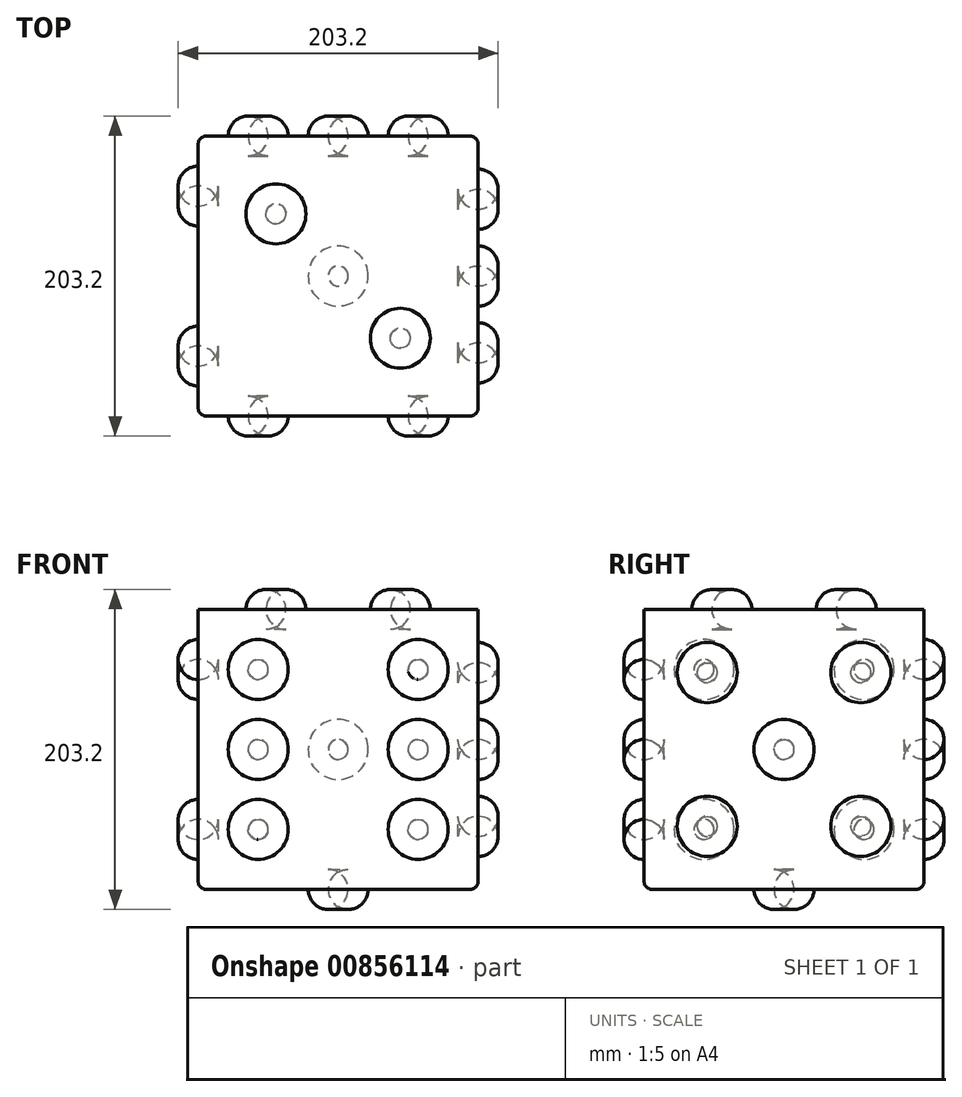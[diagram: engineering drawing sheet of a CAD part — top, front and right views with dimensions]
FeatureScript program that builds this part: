
annotation { "Feature Type Name" : "Feature", "Feature Type Description" : "" }
export const myFeature = defineFeature(function(context is Context, id is Id, definition is map)
    precondition{}
    {
        {
            var Q0;
            Q0=qCreatedBy(makeId("Top.planeOp"),FACE);
            var sketch = newSketch(context, id + "F0", { "sketchPlane" : qUnion([Q0])});
            skCircle(sketch, "E0", {"center": v(0, 0) * mm, "radius": 127 * mm});
            skSolve(sketch);
        }
        {
            var Q0;
            Q0 = qSketchRegion(id + "F0", true);
            extrude(context, id + "F1", {"entities" : qUnion([Q0]), "depth" : 177.8 * mm, "offsetDistance" : 25.4 * mm});
        }
        {
            var Q0;
            Q0=makeQuery(id+"F1.opExtrude","CAP_FACE",FACE,{"disambiguationData":[OSD([sQuery(id+"F0.wireOp",EDGE,"E0")])],"isStart":false});
            var sketch = newSketch(context, id + "F2", { "sketchPlane" : qUnion([Q0])});
            skLineSegment(sketch, "E1.bottom", {"start": v(-88.9, -88.9) * mm, "end": v(88.9, -88.9) * mm});
            skLineSegment(sketch, "E1.top", {"start": v(-88.9, 88.9) * mm, "end": v(88.9, 88.9) * mm});
            skLineSegment(sketch, "E1.left", {"start": v(-88.9, -88.9) * mm, "end": v(-88.9, 88.9) * mm});
            skLineSegment(sketch, "E1.right", {"start": v(88.9, -88.9) * mm, "end": v(88.9, 88.9) * mm});
            skPoint(sketch, "E1.middle", {"position": v(0, 0) * mm});
            skSolve(sketch);
        }
        {
            var Q0;
            {var subQ0=sQuery(id+"F2.wireOp",EDGE,"E1.top");Q0=makeQuery(id+"F2.imprint","IMPRINT",FACE,{"disambiguationData":[TD([[makeQuery(id+"F2.imprint","IMPRINT",EDGE,{"derivedFrom":subQ0}),1.0]])]});}
            var Q1;
            {var subQ0=sQuery(id+"F2.wireOp",EDGE,"E1.left");Q1=makeQuery(id+"F2.imprint","IMPRINT",FACE,{"disambiguationData":[TD([[makeQuery(id+"F2.imprint","IMPRINT",EDGE,{"derivedFrom":subQ0}),1.0]])]});}
            var Q2;
            {var subQ0=sQuery(id+"F2.wireOp",EDGE,"E1.bottom");Q2=makeQuery(id+"F2.imprint","IMPRINT",FACE,{"disambiguationData":[TD([[makeQuery(id+"F2.imprint","IMPRINT",EDGE,{"derivedFrom":subQ0}),-1.0]])]});}
            var Q3;
            {var subQ0=sQuery(id+"F2.wireOp",EDGE,"E1.right");Q3=makeQuery(id+"F2.imprint","IMPRINT",FACE,{"disambiguationData":[TD([[makeQuery(id+"F2.imprint","IMPRINT",EDGE,{"derivedFrom":subQ0}),-1.0]])]});}
            extrude(context, id + "F3", {"entities" : qUnion([Q0, Q1, Q2, Q3]), "operationType" : NewBodyOperationType.REMOVE, "endBound" : BoundingType.THROUGH_ALL, "oppositeDirection" : true, "depth" : 25.4 * mm, "offsetDistance" : 25.4 * mm});
        }
        {
            var Q0;
            Q0=makeQuery(id+"F3.boolean.opBoolean","COPY",FACE,{"derivedFrom":makeQuery(id+"F3.opExtrude","SWEPT_FACE",FACE,{"disambiguationData":[OSD([sQuery(id+"F2.wireOp",EDGE,"E1.right")])]})});
            var sketch = newSketch(context, id + "F4", { "sketchPlane" : qUnion([Q0])});
            skCircle(sketch, "E2", {"center": v(0, 88.9) * mm, "radius": 19.12 * mm});
            skCircle(sketch, "E3", {"center": v(48.8, 40.1) * mm, "radius": 19.12 * mm});
            skCircle(sketch, "E4", {"center": v(48.8, 137.7) * mm, "radius": 19.12 * mm});
            skCircle(sketch, "E5", {"center": v(-48.8, 137.7) * mm, "radius": 19.12 * mm});
            skCircle(sketch, "E6", {"center": v(-48.8, 40.1) * mm, "radius": 19.12 * mm});
            skLineSegment(sketch, "E7", {"start": v(48.8, 137.7) * mm, "end": v(-48.8, 40.1) * mm, "construction": true});
            skLineSegment(sketch, "E8", {"start": v(48.8, 40.1) * mm, "end": v(-48.8, 137.7) * mm, "construction": true});
            skSolve(sketch);
        }
        {
            var Q0;
            Q0=makeQuery(id+"F4.imprint","IMPRINT",FACE,{"disambiguationData":[TD([[makeQuery(id+"F4.imprint","IMPRINT",EDGE,{"derivedFrom":sQuery(id+"F4.wireOp",EDGE,"E5")}),1.0]])]});
            var Q1;
            Q1=makeQuery(id+"F4.imprint","IMPRINT",FACE,{"disambiguationData":[TD([[makeQuery(id+"F4.imprint","IMPRINT",EDGE,{"derivedFrom":sQuery(id+"F4.wireOp",EDGE,"E2")}),1.0]])]});
            var Q2;
            Q2=makeQuery(id+"F4.imprint","IMPRINT",FACE,{"disambiguationData":[TD([[makeQuery(id+"F4.imprint","IMPRINT",EDGE,{"derivedFrom":sQuery(id+"F4.wireOp",EDGE,"E4")}),1.0]])]});
            var Q3;
            Q3=makeQuery(id+"F4.imprint","IMPRINT",FACE,{"disambiguationData":[TD([[makeQuery(id+"F4.imprint","IMPRINT",EDGE,{"derivedFrom":sQuery(id+"F4.wireOp",EDGE,"E3")}),1.0]])]});
            var Q4;
            Q4=makeQuery(id+"F4.imprint","IMPRINT",FACE,{"disambiguationData":[TD([[makeQuery(id+"F4.imprint","IMPRINT",EDGE,{"derivedFrom":sQuery(id+"F4.wireOp",EDGE,"E6")}),1.0]])]});
            var Q5;
            Q5=sQuery(id+"F4.wireOp",EDGE,"E7");
            var Q6;
            Q6=sQuery(id+"F4.wireOp",EDGE,"E8");
            extrude(context, id + "F5", {"entities" : qUnion([Q0, Q1, Q2, Q3, Q4]), "operationType" : NewBodyOperationType.REMOVE, "surfaceEntities" : qUnion([Q5, Q6]), "oppositeDirection" : true, "depth" : 12.7 * mm, "offsetDistance" : 25.4 * mm});
        }
        {
            var Q0;
            Q0=makeQuery(id+"F3.boolean.opBoolean","COPY",FACE,{"derivedFrom":makeQuery(id+"F3.opExtrude","SWEPT_FACE",FACE,{"disambiguationData":[OSD([sQuery(id+"F2.wireOp",EDGE,"E1.bottom")])]})});
            var sketch = newSketch(context, id + "F6", { "sketchPlane" : qUnion([Q0])});
            skCircle(sketch, "E9", {"center": v(-50.8, 139.7) * mm, "radius": 19.05 * mm});
            skCircle(sketch, "E10", {"center": v(-50.8, 88.9) * mm, "radius": 19.05 * mm});
            skCircle(sketch, "E11", {"center": v(-50.8, 38.1) * mm, "radius": 19.05 * mm});
            skCircle(sketch, "E12", {"center": v(50.8, 139.7) * mm, "radius": 19.05 * mm});
            skCircle(sketch, "E13", {"center": v(50.8, 88.9) * mm, "radius": 19.05 * mm});
            skLineSegment(sketch, "E14", {"start": v(-50.8, 139.7) * mm, "end": v(-50.8, 88.9) * mm, "construction": true});
            skLineSegment(sketch, "E15", {"start": v(-50.8, 88.9) * mm, "end": v(-50.8, 38.1) * mm, "construction": true});
            skPoint(sketch, "E16", {"position": v(0, 0) * mm});
            skCircle(sketch, "E17", {"center": v(50.8, 38.1) * mm, "radius": 19.05 * mm});
            skSolve(sketch);
        }
        {
            var Q0;
            Q0=makeQuery(id+"F6.imprint","IMPRINT",FACE,{"disambiguationData":[TD([[makeQuery(id+"F6.imprint","IMPRINT",EDGE,{"derivedFrom":sQuery(id+"F6.wireOp",EDGE,"E10")}),1.0]])]});
            var Q1;
            Q1=makeQuery(id+"F6.imprint","IMPRINT",FACE,{"disambiguationData":[TD([[makeQuery(id+"F6.imprint","IMPRINT",EDGE,{"derivedFrom":sQuery(id+"F6.wireOp",EDGE,"E13")}),1.0]])]});
            var Q2;
            {var subQ0=sQuery(id+"F6.wireOp",EDGE,"E11");var subQ1=sQuery(id+"F2.wireOp",EDGE,"E1.bottom");var subQ2=makeQuery(id+"F6.imprint","INTERSECT",VERTEX,{"derivedFrom":[makeQuery(id+"F3.boolean.opBoolean","INTERSECT",EDGE,{"derivedFrom":[makeQuery(id+"F1.opExtrude","CAP_FACE",FACE,{"disambiguationData":[OSD([sQuery(id+"F0.wireOp",EDGE,"E0")])],"isStart":true}),makeQuery(id+"F3.opExtrude","SWEPT_FACE",FACE,{"disambiguationData":[OSD([subQ1])]})]}),subQ0]});Q2=makeQuery(id+"F6.imprint","IMPRINT",FACE,{"disambiguationData":[TD([[makeQuery(id+"F6.imprint","IMPRINT",EDGE,{"disambiguationData":[TD([[subQ2,1.0]])],"derivedFrom":subQ0}),1.0]])]});}
            var Q3;
            {var subQ0=sQuery(id+"F6.wireOp",EDGE,"E12");var subQ1=sQuery(id+"F2.wireOp",EDGE,"E1.bottom");var subQ2=makeQuery(id+"F6.imprint","INTERSECT",VERTEX,{"derivedFrom":[makeQuery(id+"F3.boolean.opBoolean","COPY",EDGE,{"derivedFrom":makeQuery(id+"F3.opExtrude","CAP_EDGE",EDGE,{"disambiguationData":[OSD([subQ1])],"isStart":true})}),subQ0]});Q3=makeQuery(id+"F6.imprint","IMPRINT",FACE,{"disambiguationData":[TD([[makeQuery(id+"F6.imprint","IMPRINT",EDGE,{"disambiguationData":[TD([[subQ2,1.0]])],"derivedFrom":subQ0}),1.0]])]});}
            var Q4;
            {var subQ0=sQuery(id+"F6.wireOp",EDGE,"E17");var subQ1=sQuery(id+"F2.wireOp",EDGE,"E1.bottom");var subQ2=makeQuery(id+"F6.imprint","INTERSECT",VERTEX,{"derivedFrom":[makeQuery(id+"F3.boolean.opBoolean","INTERSECT",EDGE,{"derivedFrom":[makeQuery(id+"F1.opExtrude","CAP_FACE",FACE,{"disambiguationData":[OSD([sQuery(id+"F0.wireOp",EDGE,"E0")])],"isStart":true}),makeQuery(id+"F3.opExtrude","SWEPT_FACE",FACE,{"disambiguationData":[OSD([subQ1])]})]}),subQ0]});Q4=makeQuery(id+"F6.imprint","IMPRINT",FACE,{"disambiguationData":[TD([[makeQuery(id+"F6.imprint","IMPRINT",EDGE,{"disambiguationData":[TD([[subQ2,1.0]])],"derivedFrom":subQ0}),1.0]])]});}
            var Q5;
            {var subQ0=sQuery(id+"F6.wireOp",EDGE,"E9");var subQ1=sQuery(id+"F2.wireOp",EDGE,"E1.bottom");var subQ2=makeQuery(id+"F6.imprint","INTERSECT",VERTEX,{"derivedFrom":[makeQuery(id+"F3.boolean.opBoolean","COPY",EDGE,{"derivedFrom":makeQuery(id+"F3.opExtrude","CAP_EDGE",EDGE,{"disambiguationData":[OSD([subQ1])],"isStart":true})}),subQ0]});Q5=makeQuery(id+"F6.imprint","IMPRINT",FACE,{"disambiguationData":[TD([[makeQuery(id+"F6.imprint","IMPRINT",EDGE,{"disambiguationData":[TD([[subQ2,-1.0]])],"derivedFrom":subQ0}),1.0]])]});}
            extrude(context, id + "F7", {"entities" : qUnion([Q0, Q1, Q2, Q3, Q4, Q5]), "operationType" : NewBodyOperationType.REMOVE, "oppositeDirection" : true, "depth" : 12.7 * mm, "offsetDistance" : 25.4 * mm});
        }
        {
            var Q0;
            Q0=makeQuery(id+"F3.boolean.opBoolean","COPY",FACE,{"derivedFrom":makeQuery(id+"F3.opExtrude","SWEPT_FACE",FACE,{"disambiguationData":[OSD([sQuery(id+"F2.wireOp",EDGE,"E1.left")])]})});
            var sketch = newSketch(context, id + "F8", { "sketchPlane" : qUnion([Q0])});
            skLineSegment(sketch, "E18.bottom", {"start": v(-50.8, 38.1) * mm, "end": v(50.8, 38.1) * mm, "construction": true});
            skLineSegment(sketch, "E18.top", {"start": v(-50.8, 139.7) * mm, "end": v(50.8, 139.7) * mm, "construction": true});
            skLineSegment(sketch, "E18.left", {"start": v(-50.8, 38.1) * mm, "end": v(-50.8, 139.7) * mm, "construction": true});
            skLineSegment(sketch, "E18.right", {"start": v(50.8, 38.1) * mm, "end": v(50.8, 139.7) * mm, "construction": true});
            skPoint(sketch, "E18.middle", {"position": v(0, 88.9) * mm});
            skCircle(sketch, "E19", {"center": v(50.8, 38.1) * mm, "radius": 19.05 * mm});
            skCircle(sketch, "E20", {"center": v(-50.8, 38.1) * mm, "radius": 19.05 * mm});
            skCircle(sketch, "E21", {"center": v(-50.8, 139.7) * mm, "radius": 19.05 * mm});
            skCircle(sketch, "E22", {"center": v(50.8, 139.7) * mm, "radius": 19.05 * mm});
            skSolve(sketch);
        }
        {
            var Q0;
            Q0 = qSketchRegion(id + "F8", true);
            extrude(context, id + "F9", {"entities" : qUnion([Q0]), "operationType" : NewBodyOperationType.REMOVE, "oppositeDirection" : true, "depth" : 12.7 * mm, "offsetDistance" : 25.4 * mm});
        }
        {
            var Q0;
            Q0=makeQuery(id+"F3.boolean.opBoolean","COPY",FACE,{"derivedFrom":makeQuery(id+"F3.opExtrude","SWEPT_FACE",FACE,{"disambiguationData":[OSD([sQuery(id+"F2.wireOp",EDGE,"E1.top")])]})});
            var sketch = newSketch(context, id + "F10", { "sketchPlane" : qUnion([Q0])});
            skLineSegment(sketch, "E23", {"start": v(88.9, 0) * mm, "end": v(-88.9, 177.8) * mm, "construction": true});
            skCircle(sketch, "E24", {"center": v(50.8, 38.1) * mm, "radius": 19.05 * mm});
            skCircle(sketch, "E25", {"center": v(0, 88.9) * mm, "radius": 19.05 * mm});
            skCircle(sketch, "E26", {"center": v(-50.8, 139.7) * mm, "radius": 19.05 * mm});
            skSolve(sketch);
        }
        {
            var Q0;
            Q0 = qSketchRegion(id + "F10", true);
            extrude(context, id + "F11", {"entities" : qUnion([Q0]), "operationType" : NewBodyOperationType.REMOVE, "oppositeDirection" : true, "depth" : 12.7 * mm, "offsetDistance" : 25.4 * mm});
        }
        {
            var Q0;
            Q0=makeQuery(id+"F1.opExtrude","CAP_FACE",FACE,{"disambiguationData":[OSD([sQuery(id+"F0.wireOp",EDGE,"E0")])],"isStart":true});
            var sketch = newSketch(context, id + "F12", { "sketchPlane" : qUnion([Q0])});
            skCircle(sketch, "E27", {"center": v(0, 0) * mm, "radius": 19.05 * mm});
            skSolve(sketch);
        }
        {
            var Q0;
            Q0 = qSketchRegion(id + "F12", true);
            extrude(context, id + "F13", {"entities" : qUnion([Q0]), "operationType" : NewBodyOperationType.REMOVE, "oppositeDirection" : true, "depth" : 12.7 * mm, "offsetDistance" : 25.4 * mm});
        }
        {
            var Q0;
            Q0=makeQuery(id+"F1.opExtrude","CAP_FACE",FACE,{"disambiguationData":[OSD([sQuery(id+"F0.wireOp",EDGE,"E0")])],"isStart":false});
            var sketch = newSketch(context, id + "F14", { "sketchPlane" : qUnion([Q0])});
            skLineSegment(sketch, "E28", {"start": v(-88.9, 88.9) * mm, "end": v(88.9, -88.9) * mm, "construction": true});
            skCircle(sketch, "E29", {"center": v(-39.5, 39.5) * mm, "radius": 19.05 * mm});
            skCircle(sketch, "E30", {"center": v(39.5, -39.5) * mm, "radius": 19.05 * mm});
            skSolve(sketch);
        }
        {
            var Q0;
            Q0 = qSketchRegion(id + "F14", true);
            extrude(context, id + "F15", {"entities" : qUnion([Q0]), "operationType" : NewBodyOperationType.REMOVE, "oppositeDirection" : true, "depth" : 12.7 * mm, "offsetDistance" : 25.4 * mm});
        }
        {
            var Q0;
            Q0=makeQuery(id+"F5.boolean.opBoolean","COPY",EDGE,{"derivedFrom":makeQuery(id+"F5.opExtrude","CAP_EDGE",EDGE,{"disambiguationData":[OSD([sQuery(id+"F4.wireOp",EDGE,"E5")])],"isStart":false})});
            var Q1;
            Q1=makeQuery(id+"F5.boolean.opBoolean","COPY",EDGE,{"derivedFrom":makeQuery(id+"F5.opExtrude","CAP_EDGE",EDGE,{"disambiguationData":[OSD([sQuery(id+"F4.wireOp",EDGE,"E2")])],"isStart":false})});
            var Q2;
            Q2=makeQuery(id+"F5.boolean.opBoolean","COPY",EDGE,{"derivedFrom":makeQuery(id+"F5.opExtrude","CAP_EDGE",EDGE,{"disambiguationData":[OSD([sQuery(id+"F4.wireOp",EDGE,"E4")])],"isStart":false})});
            var Q3;
            Q3=makeQuery(id+"F5.boolean.opBoolean","COPY",EDGE,{"derivedFrom":makeQuery(id+"F5.opExtrude","CAP_EDGE",EDGE,{"disambiguationData":[OSD([sQuery(id+"F4.wireOp",EDGE,"E6")])],"isStart":false})});
            var Q4;
            Q4=makeQuery(id+"F5.boolean.opBoolean","COPY",EDGE,{"derivedFrom":makeQuery(id+"F5.opExtrude","CAP_EDGE",EDGE,{"disambiguationData":[OSD([sQuery(id+"F4.wireOp",EDGE,"E3")])],"isStart":false})});
            var Q5;
            Q5=makeQuery(id+"F7.boolean.opBoolean","COPY",EDGE,{"derivedFrom":makeQuery(id+"F7.opExtrude","CAP_EDGE",EDGE,{"disambiguationData":[OSD([sQuery(id+"F6.wireOp",EDGE,"E17")])],"isStart":false})});
            var Q6;
            Q6=makeQuery(id+"F7.boolean.opBoolean","COPY",EDGE,{"derivedFrom":makeQuery(id+"F7.opExtrude","CAP_EDGE",EDGE,{"disambiguationData":[OSD([sQuery(id+"F6.wireOp",EDGE,"E11")])],"isStart":false})});
            var Q7;
            Q7=makeQuery(id+"F7.boolean.opBoolean","COPY",FACE,{"derivedFrom":makeQuery(id+"F7.opExtrude","CAP_FACE",FACE,{"disambiguationData":[OSD([sQuery(id+"F6.wireOp",EDGE,"E13")])],"isStart":false})});
            var Q8;
            Q8=makeQuery(id+"F7.boolean.opBoolean","COPY",FACE,{"derivedFrom":makeQuery(id+"F7.opExtrude","CAP_FACE",FACE,{"disambiguationData":[OSD([sQuery(id+"F6.wireOp",EDGE,"E12")])],"isStart":false})});
            var Q9;
            Q9=makeQuery(id+"F7.boolean.opBoolean","COPY",FACE,{"derivedFrom":makeQuery(id+"F7.opExtrude","CAP_FACE",FACE,{"disambiguationData":[OSD([sQuery(id+"F6.wireOp",EDGE,"E10")])],"isStart":false})});
            var Q10;
            Q10=makeQuery(id+"F7.boolean.opBoolean","COPY",FACE,{"derivedFrom":makeQuery(id+"F7.opExtrude","CAP_FACE",FACE,{"disambiguationData":[OSD([sQuery(id+"F6.wireOp",EDGE,"E9")])],"isStart":false})});
            var Q11;
            Q11=makeQuery(id+"F9.boolean.opBoolean","COPY",EDGE,{"derivedFrom":makeQuery(id+"F9.opExtrude","CAP_EDGE",EDGE,{"disambiguationData":[OSD([sQuery(id+"F8.wireOp",EDGE,"E19")])],"isStart":false})});
            var Q12;
            Q12=makeQuery(id+"F9.boolean.opBoolean","COPY",FACE,{"derivedFrom":makeQuery(id+"F9.opExtrude","CAP_FACE",FACE,{"disambiguationData":[OSD([sQuery(id+"F8.wireOp",EDGE,"E20")])],"isStart":false})});
            var Q13;
            Q13=makeQuery(id+"F9.boolean.opBoolean","COPY",FACE,{"derivedFrom":makeQuery(id+"F9.opExtrude","CAP_FACE",FACE,{"disambiguationData":[OSD([sQuery(id+"F8.wireOp",EDGE,"E21")])],"isStart":false})});
            var Q14;
            Q14=makeQuery(id+"F9.boolean.opBoolean","COPY",FACE,{"derivedFrom":makeQuery(id+"F9.opExtrude","CAP_FACE",FACE,{"disambiguationData":[OSD([sQuery(id+"F8.wireOp",EDGE,"E22")])],"isStart":false})});
            var Q15;
            Q15=makeQuery(id+"F11.boolean.opBoolean","COPY",FACE,{"derivedFrom":makeQuery(id+"F11.opExtrude","CAP_FACE",FACE,{"disambiguationData":[OSD([sQuery(id+"F10.wireOp",EDGE,"E25")])],"isStart":false})});
            var Q16;
            Q16=makeQuery(id+"F11.boolean.opBoolean","COPY",FACE,{"derivedFrom":makeQuery(id+"F11.opExtrude","CAP_FACE",FACE,{"disambiguationData":[OSD([sQuery(id+"F10.wireOp",EDGE,"E26")])],"isStart":false})});
            var Q17;
            Q17=makeQuery(id+"F11.boolean.opBoolean","COPY",FACE,{"derivedFrom":makeQuery(id+"F11.opExtrude","CAP_FACE",FACE,{"disambiguationData":[OSD([sQuery(id+"F10.wireOp",EDGE,"E24")])],"isStart":false})});
            var Q18;
            Q18=makeQuery(id+"F13.boolean.opBoolean","COPY",EDGE,{"derivedFrom":makeQuery(id+"F13.opExtrude","CAP_EDGE",EDGE,{"disambiguationData":[OSD([sQuery(id+"F12.wireOp",EDGE,"E27")])],"isStart":false})});
            var Q19;
            Q19=makeQuery(id+"F15.boolean.opBoolean","COPY",FACE,{"derivedFrom":makeQuery(id+"F15.opExtrude","CAP_FACE",FACE,{"disambiguationData":[OSD([sQuery(id+"F14.wireOp",EDGE,"E29")])],"isStart":false})});
            var Q20;
            Q20=makeQuery(id+"F15.boolean.opBoolean","COPY",FACE,{"derivedFrom":makeQuery(id+"F15.opExtrude","CAP_FACE",FACE,{"disambiguationData":[OSD([sQuery(id+"F14.wireOp",EDGE,"E30")])],"isStart":false})});
            fillet(context, id + "F16", {"entities" : qUnion([Q0, Q1, Q2, Q3, Q4, Q5, Q6, Q7, Q8, Q9, Q10, Q11, Q12, Q13, Q14, Q15, Q16, Q17, Q18, Q19, Q20]), "radius" : 12.7 * mm, "tangentPropagation" : true, "allowEdgeOverflow" : false});
        }
        {
            var Q0;
            Q0=makeQuery(id+"F3.boolean.opBoolean","COPY",EDGE,{"derivedFrom":makeQuery(id+"F3.opExtrude","CAP_EDGE",EDGE,{"disambiguationData":[OSD([sQuery(id+"F2.wireOp",EDGE,"E1.bottom")])],"isStart":true})});
            var Q1;
            Q1=makeQuery(id+"F3.boolean.opBoolean","COPY",EDGE,{"derivedFrom":makeQuery(id+"F3.opExtrude","CAP_EDGE",EDGE,{"disambiguationData":[OSD([sQuery(id+"F2.wireOp",EDGE,"E1.right")])],"isStart":true})});
            var Q2;
            Q2=makeQuery(id+"F3.boolean.opBoolean","COPY",EDGE,{"derivedFrom":makeQuery(id+"F3.opExtrude","SWEPT_EDGE",EDGE,{"disambiguationData":[OSD([sQuery(id+"F2.wireOp",EDGE,"E1.bottom"),sQuery(id+"F2.wireOp",EDGE,"E1.right")])]})});
            var Q3;
            Q3=makeQuery(id+"F3.boolean.opBoolean","COPY",EDGE,{"derivedFrom":makeQuery(id+"F3.opExtrude","CAP_EDGE",EDGE,{"disambiguationData":[OSD([sQuery(id+"F2.wireOp",EDGE,"E1.top")])],"isStart":true})});
            var Q4;
            Q4=makeQuery(id+"F3.boolean.opBoolean","COPY",EDGE,{"derivedFrom":makeQuery(id+"F3.opExtrude","CAP_EDGE",EDGE,{"disambiguationData":[OSD([sQuery(id+"F2.wireOp",EDGE,"E1.left")])],"isStart":true})});
            var Q5;
            Q5=makeQuery(id+"F3.boolean.opBoolean","COPY",EDGE,{"derivedFrom":makeQuery(id+"F3.opExtrude","SWEPT_EDGE",EDGE,{"disambiguationData":[OSD([sQuery(id+"F2.wireOp",EDGE,"E1.bottom"),sQuery(id+"F2.wireOp",EDGE,"E1.left")])]})});
            var Q6;
            Q6=makeQuery(id+"F3.boolean.opBoolean","COPY",EDGE,{"derivedFrom":makeQuery(id+"F3.opExtrude","SWEPT_EDGE",EDGE,{"disambiguationData":[OSD([sQuery(id+"F2.wireOp",EDGE,"E1.top"),sQuery(id+"F2.wireOp",EDGE,"E1.left")])]})});
            var Q7;
            Q7=makeQuery(id+"F3.boolean.opBoolean","INTERSECT",EDGE,{"derivedFrom":[makeQuery(id+"F1.opExtrude","CAP_FACE",FACE,{"disambiguationData":[OSD([sQuery(id+"F0.wireOp",EDGE,"E0")])],"isStart":true}),makeQuery(id+"F3.opExtrude","SWEPT_FACE",FACE,{"disambiguationData":[OSD([sQuery(id+"F2.wireOp",EDGE,"E1.left")])]})]});
            var Q8;
            Q8=makeQuery(id+"F3.boolean.opBoolean","INTERSECT",EDGE,{"derivedFrom":[makeQuery(id+"F1.opExtrude","CAP_FACE",FACE,{"disambiguationData":[OSD([sQuery(id+"F0.wireOp",EDGE,"E0")])],"isStart":true}),makeQuery(id+"F3.opExtrude","SWEPT_FACE",FACE,{"disambiguationData":[OSD([sQuery(id+"F2.wireOp",EDGE,"E1.bottom")])]})]});
            var Q9;
            Q9=makeQuery(id+"F3.boolean.opBoolean","INTERSECT",EDGE,{"derivedFrom":[makeQuery(id+"F1.opExtrude","CAP_FACE",FACE,{"disambiguationData":[OSD([sQuery(id+"F0.wireOp",EDGE,"E0")])],"isStart":true}),makeQuery(id+"F3.opExtrude","SWEPT_FACE",FACE,{"disambiguationData":[OSD([sQuery(id+"F2.wireOp",EDGE,"E1.right")])]})]});
            var Q10;
            Q10=makeQuery(id+"F3.boolean.opBoolean","INTERSECT",EDGE,{"derivedFrom":[makeQuery(id+"F1.opExtrude","CAP_FACE",FACE,{"disambiguationData":[OSD([sQuery(id+"F0.wireOp",EDGE,"E0")])],"isStart":true}),makeQuery(id+"F3.opExtrude","SWEPT_FACE",FACE,{"disambiguationData":[OSD([sQuery(id+"F2.wireOp",EDGE,"E1.top")])]})]});
            var Q11;
            Q11=makeQuery(id+"F3.boolean.opBoolean","COPY",EDGE,{"derivedFrom":makeQuery(id+"F3.opExtrude","SWEPT_EDGE",EDGE,{"disambiguationData":[OSD([sQuery(id+"F2.wireOp",EDGE,"E1.top"),sQuery(id+"F2.wireOp",EDGE,"E1.right")])]})});
            fillet(context, id + "F17", {"entities" : qUnion([Q0, Q1, Q2, Q3, Q4, Q5, Q6, Q7, Q8, Q9, Q10, Q11]), "radius" : 5.08 * mm, "tangentPropagation" : true, "allowEdgeOverflow" : false});
        }
    });
